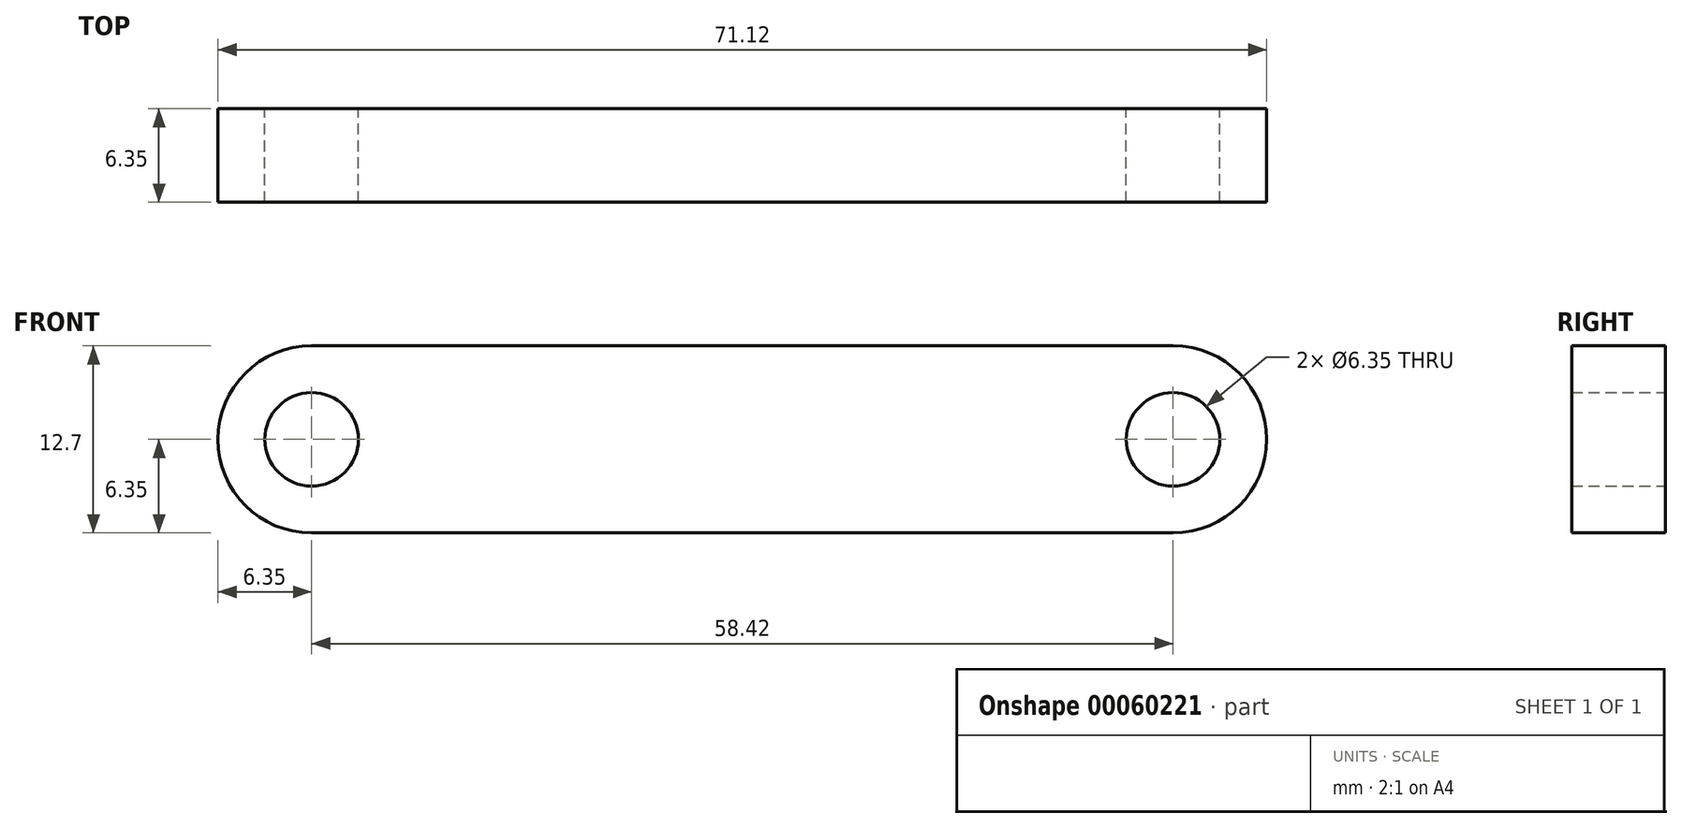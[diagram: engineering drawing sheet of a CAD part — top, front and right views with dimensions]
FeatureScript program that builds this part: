
annotation { "Feature Type Name" : "Feature", "Feature Type Description" : "" }
export const myFeature = defineFeature(function(context is Context, id is Id, definition is map)
    precondition{}
    {
        {
            var Q0;
            Q0=qCreatedBy(makeId("Front.planeOp"),FACE);
            var sketch = newSketch(context, id + "F0", { "sketchPlane" : qUnion([Q0])});
            skCircle(sketch, "E0", {"center": v(-29.21, 0) * mm, "radius": 3.18 * mm});
            skArc(sketch, "E1", {"start": v(-29.21, 6.35) * mm, "mid": v(-35.56, 0) * mm, "end": v(-29.21, -6.35) * mm});
            skCircle(sketch, "E2", {"center": v(29.21, 0) * mm, "radius": 3.18 * mm});
            skArc(sketch, "E3", {"start": v(29.21, -6.35) * mm, "mid": v(35.56, 0) * mm, "end": v(29.21, 6.35) * mm});
            skLineSegment(sketch, "E4", {"start": v(-29.21, -6.35) * mm, "end": v(29.21, -6.35) * mm});
            skLineSegment(sketch, "E5", {"start": v(-29.21, 6.35) * mm, "end": v(29.21, 6.35) * mm});
            skSolve(sketch);
        }
        {
            var Q0;
            Q0 = qSketchRegion(id + "F0", true);
            extrude(context, id + "F1", {"entities" : qUnion([Q0]), "depth" : 6.35 * mm});
        }
    });
